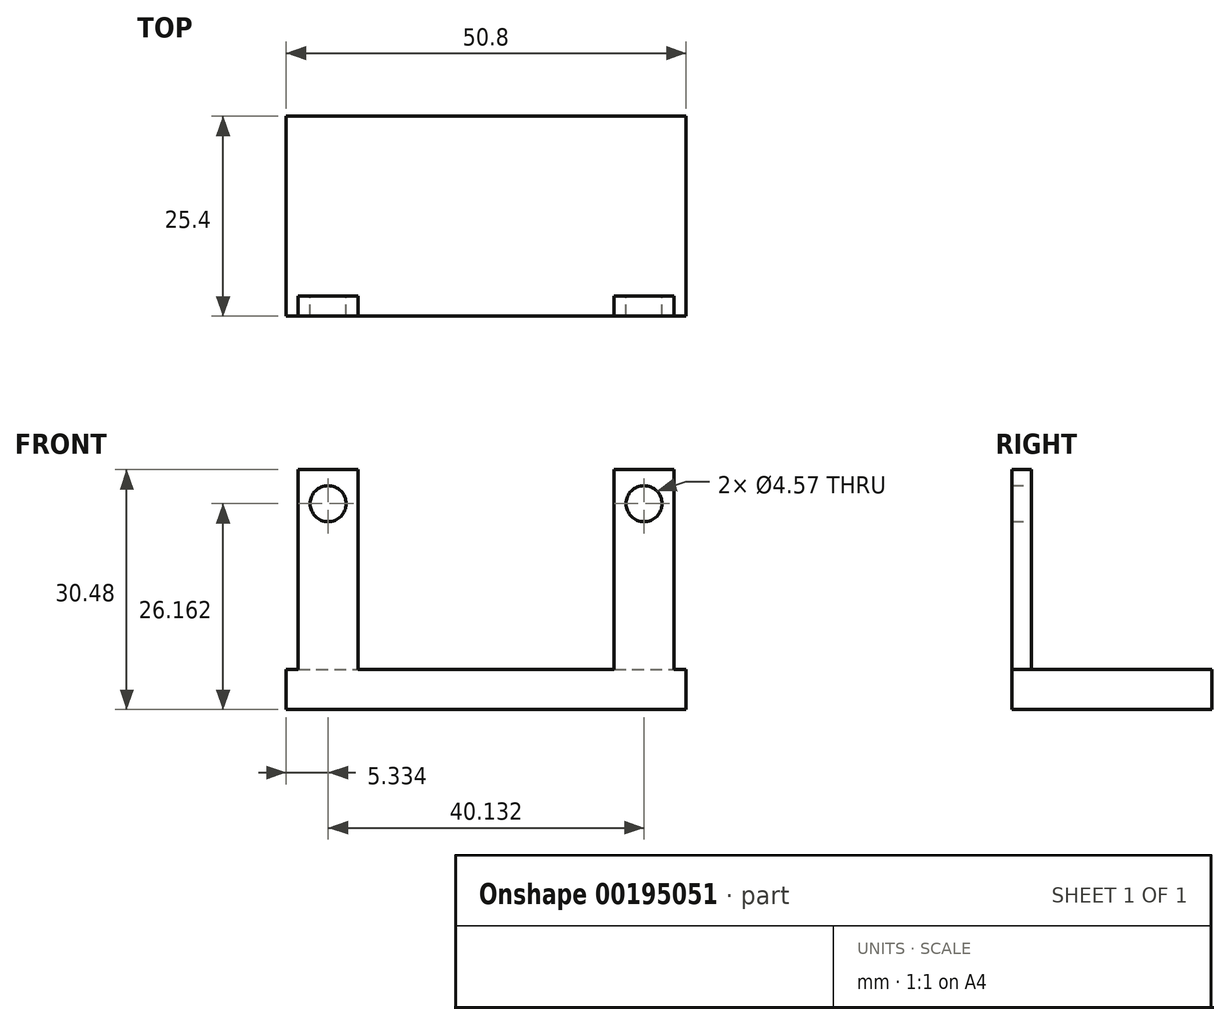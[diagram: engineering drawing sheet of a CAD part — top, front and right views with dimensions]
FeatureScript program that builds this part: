
annotation { "Feature Type Name" : "Feature", "Feature Type Description" : "" }
export const myFeature = defineFeature(function(context is Context, id is Id, definition is map)
    precondition{}
    {
        {
            var Q0;
            Q0=qCreatedBy(makeId("Top.planeOp"),FACE);
            var sketch = newSketch(context, id + "F0", { "sketchPlane" : qUnion([Q0])});
            skLineSegment(sketch, "E0.bottom", {"start": v(-25.4, 12.7) * mm, "end": v(25.4, 12.7) * mm});
            skLineSegment(sketch, "E0.top", {"start": v(-25.4, -12.7) * mm, "end": v(25.4, -12.7) * mm});
            skLineSegment(sketch, "E0.left", {"start": v(-25.4, 12.7) * mm, "end": v(-25.4, -12.7) * mm});
            skLineSegment(sketch, "E0.right", {"start": v(25.4, 12.7) * mm, "end": v(25.4, -12.7) * mm});
            skLineSegment(sketch, "E1.bottom", {"start": v(-23.88, -10.16) * mm, "end": v(-16.26, -10.16) * mm});
            skLineSegment(sketch, "E1.top", {"start": v(-23.88, -12.7) * mm, "end": v(-16.26, -12.7) * mm});
            skLineSegment(sketch, "E1.left", {"start": v(-23.88, -10.16) * mm, "end": v(-23.88, -12.7) * mm});
            skLineSegment(sketch, "E1.right", {"start": v(-16.26, -10.16) * mm, "end": v(-16.26, -12.7) * mm});
            skLineSegment(sketch, "E2.bottom", {"start": v(16.26, -10.16) * mm, "end": v(23.88, -10.16) * mm});
            skLineSegment(sketch, "E2.top", {"start": v(16.26, -12.7) * mm, "end": v(23.88, -12.7) * mm});
            skLineSegment(sketch, "E2.left", {"start": v(16.26, -10.16) * mm, "end": v(16.26, -12.7) * mm});
            skLineSegment(sketch, "E2.right", {"start": v(23.88, -10.16) * mm, "end": v(23.88, -12.7) * mm});
            skSolve(sketch);
        }
        {
            var Q0;
            Q0=makeQuery(id+"F0.imprint","IMPRINT",FACE,{"disambiguationData":[TD([[makeQuery(id+"F0.imprint","IMPRINT",EDGE,{"derivedFrom":sQuery(id+"F0.wireOp",EDGE,"E0.bottom")}),-1.0]])]});
            extrude(context, id + "F1", {"entities" : qUnion([Q0]), "depth" : 5.08 * mm});
        }
        {
            var Q0;
            Q0=makeQuery(id+"F0.imprint","IMPRINT",FACE,{"disambiguationData":[TD([[makeQuery(id+"F0.imprint","IMPRINT",EDGE,{"derivedFrom":sQuery(id+"F0.wireOp",EDGE,"E1.bottom")}),-1.0]])]});
            var Q1;
            Q1=makeQuery(id+"F0.imprint","IMPRINT",FACE,{"disambiguationData":[TD([[makeQuery(id+"F0.imprint","IMPRINT",EDGE,{"derivedFrom":sQuery(id+"F0.wireOp",EDGE,"E2.bottom")}),-1.0]])]});
            extrude(context, id + "F2", {"entities" : qUnion([Q0, Q1]), "operationType" : NewBodyOperationType.ADD, "depth" : 30.48 * mm});
        }
        {
            var Q0;
            Q0=makeQuery(id+"F2.opExtrude","SWEPT_FACE",FACE,{"disambiguationData":[OSD([sQuery(id+"F0.wireOp",EDGE,"E2.bottom")])]});
            var sketch = newSketch(context, id + "F3", { "sketchPlane" : qUnion([Q0])});
            skCircle(sketch, "E3", {"center": v(-20.07, 26.16) * mm, "radius": 2.29 * mm});
            skCircle(sketch, "E4", {"center": v(20.07, 26.16) * mm, "radius": 2.29 * mm});
            skSolve(sketch);
        }
        {
            var Q0;
            Q0=makeQuery(id+"F3.imprint","IMPRINT",FACE,{"disambiguationData":[TD([[makeQuery(id+"F3.imprint","IMPRINT",EDGE,{"derivedFrom":sQuery(id+"F3.wireOp",EDGE,"E3")}),1.0]])]});
            var Q1;
            Q1=makeQuery(id+"F3.imprint","IMPRINT",FACE,{"disambiguationData":[TD([[makeQuery(id+"F3.imprint","IMPRINT",EDGE,{"derivedFrom":sQuery(id+"F3.wireOp",EDGE,"E4")}),1.0]])]});
            extrude(context, id + "F4", {"entities" : qUnion([Q0, Q1]), "operationType" : NewBodyOperationType.REMOVE, "oppositeDirection" : true, "depth" : 7.11 * mm});
        }
    });
